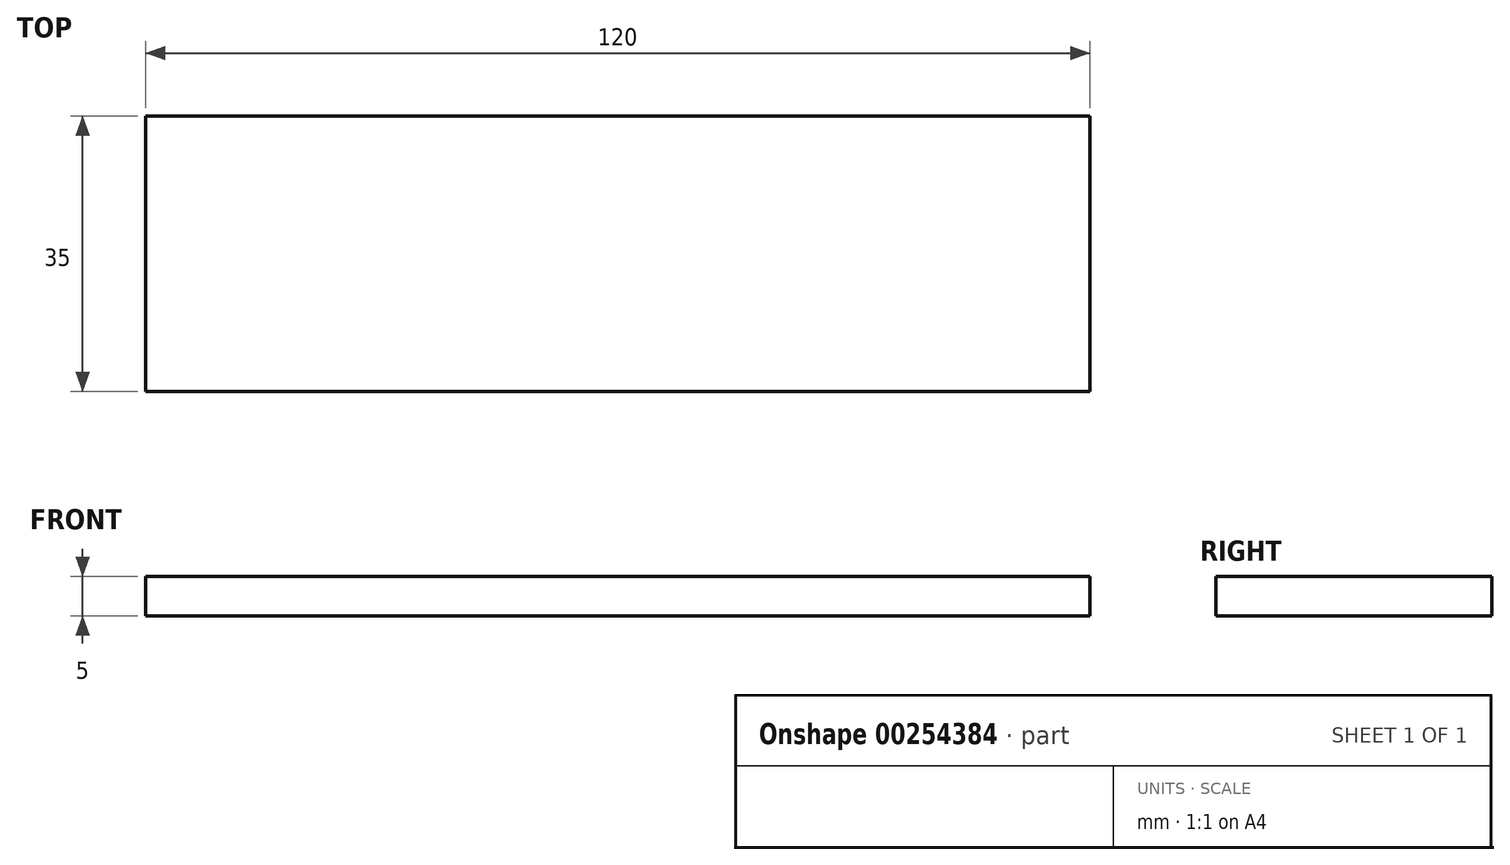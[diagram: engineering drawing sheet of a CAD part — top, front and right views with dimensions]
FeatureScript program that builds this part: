
annotation { "Feature Type Name" : "Feature", "Feature Type Description" : "" }
export const myFeature = defineFeature(function(context is Context, id is Id, definition is map)
    precondition{}
    {
        {
            var Q0;
            Q0=qCreatedBy(makeId("Top.planeOp"),FACE);
            var sketch = newSketch(context, id + "F0", { "sketchPlane" : qUnion([Q0])});
            skLineSegment(sketch, "E0.bottom", {"start": v(-60, 17.5) * mm, "end": v(60, 17.5) * mm});
            skLineSegment(sketch, "E0.top", {"start": v(-60, -17.5) * mm, "end": v(60, -17.5) * mm});
            skLineSegment(sketch, "E0.left", {"start": v(-60, 17.5) * mm, "end": v(-60, -17.5) * mm});
            skLineSegment(sketch, "E0.right", {"start": v(60, 17.5) * mm, "end": v(60, -17.5) * mm});
            skPoint(sketch, "E0.middle", {"position": v(0, 0) * mm});
            skSolve(sketch);
        }
        {
            var Q0;
            Q0 = qSketchRegion(id + "F0", true);
            extrude(context, id + "F1", {"entities" : qUnion([Q0]), "depth" : 5 * mm});
        }
    });
